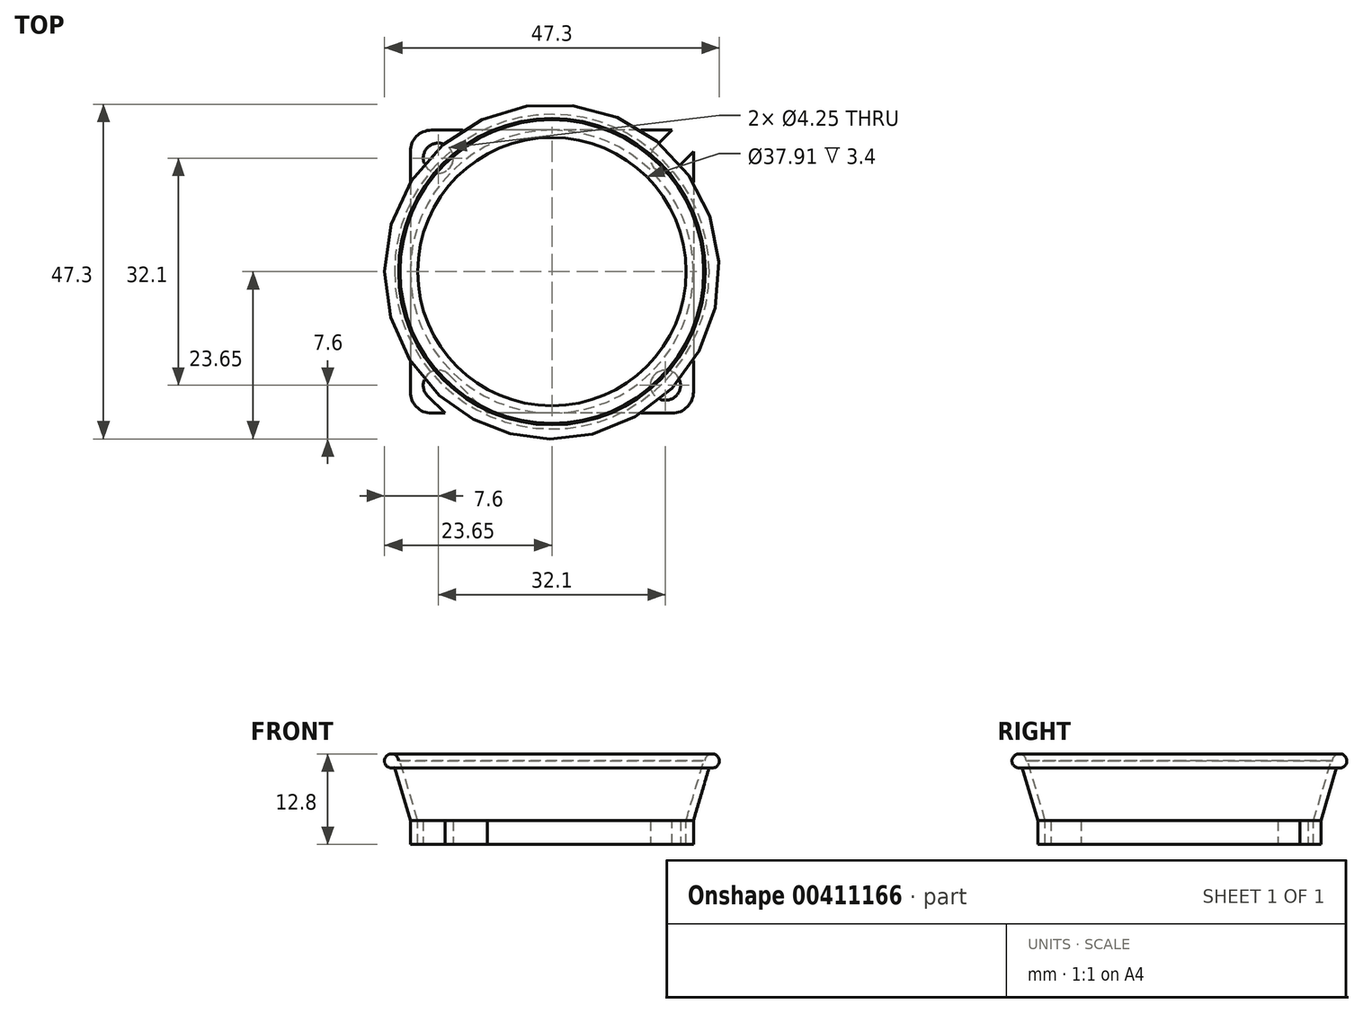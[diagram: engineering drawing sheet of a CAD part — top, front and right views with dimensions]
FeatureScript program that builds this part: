
annotation { "Feature Type Name" : "Feature", "Feature Type Description" : "" }
export const myFeature = defineFeature(function(context is Context, id is Id, definition is map)
    precondition{}
    {
        {
            var Q0;
            Q0=qCreatedBy(makeId("Top.planeOp"),FACE);
            var sketch = newSketch(context, id + "F0", { "sketchPlane" : qUnion([Q0])});
            skCircle(sketch, "E0", {"center": v(0, 0) * mm, "radius": 20 * mm});
            skSolve(sketch);
        }
        {
            var Q0;
            Q0=qCreatedBy(makeId("Right.planeOp"),FACE);
            var sketch = newSketch(context, id + "F1", { "sketchPlane" : qUnion([Q0])});
            skLineSegment(sketch, "E1", {"start": v(0, 0) * mm, "end": v(0, 8.4) * mm});
            skSolve(sketch);
        }
        {
            var Q0;
            Q0=qCreatedBy(makeId("Top.planeOp"),FACE);
            var Q1;
            Q1=sQuery(id+"F1.wireOp",VERTEX,"E1.end");
            cPlane(context, id + "F2", {"entities" : qUnion([Q0, Q1]), "cplaneType" : CPlaneType.PLANE_POINT, "offset" : 25 * mm, "width" : 150 * mm, "height" : 150 * mm});
        }
        {
            var Q0;
            Q0=qCreatedBy(id+"F2.planeOp",FACE);
            var sketch = newSketch(context, id + "F3", { "sketchPlane" : qUnion([Q0])});
            skCircle(sketch, "E2", {"center": v(0, 0) * mm, "radius": 22.5 * mm});
            skSolve(sketch);
        }
        {
            var Q0;
            Q0=makeQuery(id+"F3.imprint","IMPRINT",FACE,{"disambiguationData":[TD([[makeQuery(id+"F3.imprint","IMPRINT",EDGE,{"derivedFrom":sQuery(id+"F3.wireOp",EDGE,"E2")}),1.0]])]});
            var Q1;
            Q1=makeQuery(id+"F0.imprint","IMPRINT",FACE,{"disambiguationData":[TD([[makeQuery(id+"F0.imprint","IMPRINT",EDGE,{"derivedFrom":sQuery(id+"F0.wireOp",EDGE,"E0")}),1.0]])]});
            loft(context, id + "F4", {"sheetProfilesArray" : [{ "sheetProfileEntities" : qUnion([Q0]) }, { "sheetProfileEntities" : qUnion([Q1]) }]});
        }
        {
            var Q0;
            Q0=qCreatedBy(makeId("Right.planeOp"),FACE);
            var sketch = newSketch(context, id + "F5", { "sketchPlane" : qUnion([Q0])});
            skCircle(sketch, "E3", {"center": v(-22.65, 8.4) * mm, "radius": 1 * mm});
            skSolve(sketch);
        }
        {
            var Q0;
            Q0 = qSketchRegion(id + "F5", true);
            var Q1;
            Q1=sQuery(id+"F1.wireOp",EDGE,"E1");
            revolve(context, id + "F6", {"operationType" : NewBodyOperationType.ADD, "entities" : qUnion([Q0]), "axis" : qUnion([Q1]), "revolveType" : RevolveType.FULL});
        }
        {
            var Q0;
            Q0=makeQuery(id+"F4.opLoft","CAP_FACE",FACE,{"disambiguationData":[OSD([makeQuery(id+"F3.imprint","IMPRINT",FACE,{"disambiguationData":[TD([[makeQuery(id+"F3.imprint","IMPRINT",EDGE,{"derivedFrom":sQuery(id+"F3.wireOp",EDGE,"E2")}),1.0]])]})])],"isStart":true});
            var Q1;
            Q1=makeQuery(id+"F4.opLoft","CAP_FACE",FACE,{"disambiguationData":[OSD([makeQuery(id+"F0.imprint","IMPRINT",FACE,{"disambiguationData":[TD([[makeQuery(id+"F0.imprint","IMPRINT",EDGE,{"derivedFrom":sQuery(id+"F0.wireOp",EDGE,"E0")}),1.0]])]})])],"isStart":true});
            shell(context, id + "F7", {"entities" : qUnion([Q0, Q1]), "thickness" : 1 * mm});
        }
        {
            var Q0;
            Q0=qCreatedBy(makeId("Top.planeOp"),FACE);
            var sketch = newSketch(context, id + "F8", { "sketchPlane" : qUnion([Q0])});
            skLineSegment(sketch, "E4.bottom", {"start": v(20, 20) * mm, "end": v(-20, 20) * mm});
            skLineSegment(sketch, "E4.top", {"start": v(20, -20) * mm, "end": v(-20, -20) * mm});
            skLineSegment(sketch, "E4.left", {"start": v(20, 20) * mm, "end": v(20, -20) * mm});
            skLineSegment(sketch, "E4.right", {"start": v(-20, 20) * mm, "end": v(-20, -20) * mm});
            skPoint(sketch, "E4.middle", {"position": v(0, 0) * mm});
            skSolve(sketch);
        }
        {
            var Q0;
            Q0 = qSketchRegion(id + "F8", true);
            extrude(context, id + "F9", {"entities" : qUnion([Q0]), "operationType" : NewBodyOperationType.ADD, "oppositeDirection" : true, "depth" : 3.4 * mm});
        }
        {
            var Q0;
            Q0=makeQuery(id+"F9.opExtrude","CAP_FACE",FACE,{"disambiguationData":[OSD([sQuery(id+"F8.wireOp",EDGE,"E4.bottom"),sQuery(id+"F8.wireOp",EDGE,"E4.top"),sQuery(id+"F8.wireOp",EDGE,"E4.left"),sQuery(id+"F8.wireOp",EDGE,"E4.right")])],"isStart":false});
            var sketch = newSketch(context, id + "F10", { "sketchPlane" : qUnion([Q0])});
            skCircle(sketch, "E5", {"center": v(16.05, -16.05) * mm, "radius": 2.12 * mm});
            skCircle(sketch, "E6", {"center": v(-16.05, -16.05) * mm, "radius": 2.12 * mm});
            skCircle(sketch, "E7", {"center": v(16.05, 16.05) * mm, "radius": 2.12 * mm});
            skCircle(sketch, "E8", {"center": v(-16.05, 16.05) * mm, "radius": 2.12 * mm});
            skLineSegment(sketch, "E9", {"start": v(-16.05, 16.05) * mm, "end": v(-16.05, -16.05) * mm, "construction": true});
            skLineSegment(sketch, "E10", {"start": v(-16.05, -16.05) * mm, "end": v(16.05, -16.05) * mm, "construction": true});
            skLineSegment(sketch, "E11", {"start": v(-16.05, 0) * mm, "end": v(-12.03, 0) * mm, "construction": true});
            skLineSegment(sketch, "E12", {"start": v(0, -16.05) * mm, "end": v(0, -13.09) * mm, "construction": true});
            skLineSegment(sketch, "E13", {"start": v(-16.05, 16.05) * mm, "end": v(16.05, 16.05) * mm, "construction": true});
            skSolve(sketch);
        }
        {
            var Q0;
            Q0 = qSketchRegion(id + "F10", true);
            extrude(context, id + "F11", {"entities" : qUnion([Q0]), "operationType" : NewBodyOperationType.REMOVE, "oppositeDirection" : true, "depth" : 4 * mm});
        }
        {
            var Q0;
            Q0=makeQuery(id+"F9.boolean.opBoolean","SPLIT",FACE,{"disambiguationData":[TD([makeQuery(id+"F7.opShell","OFFSET_FACE",FACE,{"disambiguationData":[OSD([sQuery(id+"F0.wireOp",EDGE,"E0"),sQuery(id+"F3.wireOp",EDGE,"E2")])]})])],"derivedFrom":makeQuery(id+"F9.opExtrude","CAP_FACE",FACE,{"disambiguationData":[OSD([sQuery(id+"F8.wireOp",EDGE,"E4.bottom"),sQuery(id+"F8.wireOp",EDGE,"E4.top"),sQuery(id+"F8.wireOp",EDGE,"E4.left"),sQuery(id+"F8.wireOp",EDGE,"E4.right")])],"isStart":true})});
            var sketch = newSketch(context, id + "F12", { "sketchPlane" : qUnion([Q0])});
            skCircle(sketch, "E14.0", {"center": v(0, 0) * mm, "radius": 18.96 * mm});
            skSolve(sketch);
        }
        {
            var Q0;
            Q0 = qSketchRegion(id + "F12", true);
            extrude(context, id + "F13", {"entities" : qUnion([Q0]), "operationType" : NewBodyOperationType.REMOVE, "endBound" : BoundingType.THROUGH_ALL, "oppositeDirection" : true, "depth" : 25 * mm});
        }
        {
            var Q0;
            Q0=makeQuery(id+"F9.opExtrude","SWEPT_EDGE",EDGE,{"disambiguationData":[OSD([sQuery(id+"F8.wireOp",EDGE,"E4.bottom"),sQuery(id+"F8.wireOp",EDGE,"E4.right")])]});
            var Q1;
            Q1=makeQuery(id+"F9.opExtrude","SWEPT_EDGE",EDGE,{"disambiguationData":[OSD([sQuery(id+"F8.wireOp",EDGE,"E4.top"),sQuery(id+"F8.wireOp",EDGE,"E4.right")])]});
            var Q2;
            Q2=makeQuery(id+"F9.opExtrude","SWEPT_EDGE",EDGE,{"disambiguationData":[OSD([sQuery(id+"F8.wireOp",EDGE,"E4.top"),sQuery(id+"F8.wireOp",EDGE,"E4.left")])]});
            var Q3;
            Q3=makeQuery(id+"F9.opExtrude","SWEPT_EDGE",EDGE,{"disambiguationData":[OSD([sQuery(id+"F8.wireOp",EDGE,"E4.bottom"),sQuery(id+"F8.wireOp",EDGE,"E4.left")])]});
            fillet(context, id + "F14", {"entities" : qUnion([Q0, Q1, Q2, Q3]), "radius" : 3 * mm, "tangentPropagation" : true, "allowEdgeOverflow" : false});
        }
        {
            var Q0;
            {var subQ0=sQuery(id+"F8.wireOp",EDGE,"E4.bottom");var subQ1=sQuery(id+"F8.wireOp",EDGE,"E4.left");var subQ2=makeQuery(id+"F9.opExtrude","CAP_FACE",FACE,{"disambiguationData":[OSD([subQ0,sQuery(id+"F8.wireOp",EDGE,"E4.top"),subQ1,sQuery(id+"F8.wireOp",EDGE,"E4.right")])],"isStart":true});Q0=makeQuery(id+"F9.boolean.opBoolean","SPLIT",FACE,{"disambiguationData":[TD([makeQuery(id+"F4.opLoft","SWEPT_FACE",FACE,{"disambiguationData":[OSD([sQuery(id+"F0.wireOp",EDGE,"E0"),sQuery(id+"F3.wireOp",EDGE,"E2")])]}),makeQuery(id+"F9.opExtrude","SWEPT_FACE",FACE,{"disambiguationData":[OSD([subQ0])]}),subQ2,makeQuery(id+"F9.opExtrude","SWEPT_FACE",FACE,{"disambiguationData":[OSD([subQ1])]})])],"derivedFrom":subQ2});}
            var sketch = newSketch(context, id + "F15", { "sketchPlane" : qUnion([Q0])});
            skLineSegment(sketch, "E15", {"start": v(17.55, 14.55) * mm, "end": v(20, 17) * mm});
            skLineSegment(sketch, "E16", {"start": v(14.55, 17.55) * mm, "end": v(16.99, 20) * mm});
            skPoint(sketch, "E17.orphan", {"position": v(20, 0) * mm});
            skPoint(sketch, "E18.0.end.orphan", {"position": v(0, 20) * mm});
            skArc(sketch, "E19.0", {"start": v(20, 17) * mm, "mid": v(19.12, 19.12) * mm, "end": v(17, 20) * mm});
            skSolve(sketch);
        }
        {
            var Q0;
            {var subQ9=sQuery(id+"F15.wireOp",EDGE,"E15");Q0=makeQuery(id+"F15.imprint","IMPRINT",FACE,{"disambiguationData":[TD([[makeQuery(id+"F15.imprint","IMPRINT",EDGE,{"derivedFrom":subQ9}),1.0]])]});}
            extrude(context, id + "F16", {"entities" : qUnion([Q0]), "operationType" : NewBodyOperationType.REMOVE, "oppositeDirection" : true, "depth" : 4 * mm});
        }
        {
            var Q0;
            {var subQ0=sQuery(id+"F8.wireOp",EDGE,"E4.right");var subQ1=sQuery(id+"F8.wireOp",EDGE,"E4.top");var subQ2=makeQuery(id+"F9.opExtrude","CAP_FACE",FACE,{"disambiguationData":[OSD([sQuery(id+"F8.wireOp",EDGE,"E4.bottom"),subQ1,sQuery(id+"F8.wireOp",EDGE,"E4.left"),subQ0])],"isStart":true});Q0=makeQuery(id+"F9.boolean.opBoolean","SPLIT",FACE,{"disambiguationData":[TD([makeQuery(id+"F4.opLoft","SWEPT_FACE",FACE,{"disambiguationData":[OSD([sQuery(id+"F0.wireOp",EDGE,"E0"),sQuery(id+"F3.wireOp",EDGE,"E2")])]}),subQ2,makeQuery(id+"F9.opExtrude","SWEPT_FACE",FACE,{"disambiguationData":[OSD([subQ1])]}),makeQuery(id+"F9.opExtrude","SWEPT_FACE",FACE,{"disambiguationData":[OSD([subQ0])]})])],"derivedFrom":subQ2});}
            var sketch = newSketch(context, id + "F17", { "sketchPlane" : qUnion([Q0])});
            skLineSegment(sketch, "E20", {"start": v(-17.55, -17.55) * mm, "end": v(-15.1, -20) * mm});
            skLineSegment(sketch, "E21", {"start": v(-14.55, -14.55) * mm, "end": v(-9.1, -20) * mm});
            skLineSegment(sketch, "E22", {"start": v(-14.55, -14.55) * mm, "end": v(-17.55, -17.55) * mm});
            skLineSegment(sketch, "E23", {"start": v(-9.1, -20) * mm, "end": v(-15.1, -20) * mm});
            skSolve(sketch);
        }
        {
            var Q0;
            Q0 = qSketchRegion(id + "F17", true);
            extrude(context, id + "F18", {"entities" : qUnion([Q0]), "operationType" : NewBodyOperationType.REMOVE, "oppositeDirection" : true, "depth" : 25 * mm});
        }
    });
